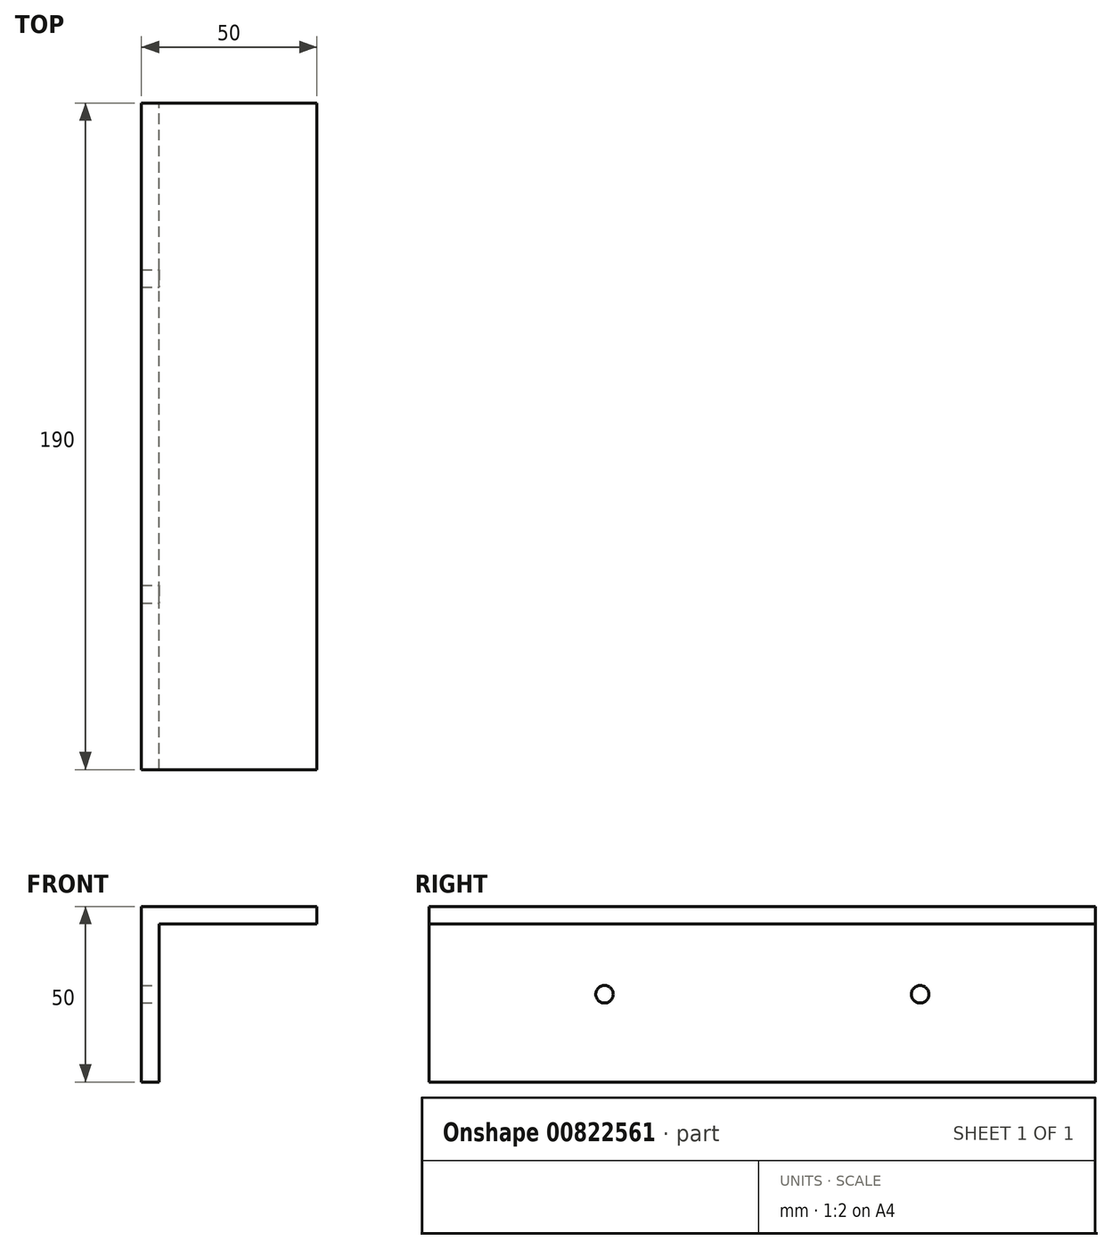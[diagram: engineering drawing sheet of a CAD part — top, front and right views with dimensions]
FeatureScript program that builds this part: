
annotation { "Feature Type Name" : "Feature", "Feature Type Description" : "" }
export const myFeature = defineFeature(function(context is Context, id is Id, definition is map)
    precondition{}
    {
        {
            var Q0;
            Q0=qCreatedBy(makeId("Front.planeOp"),FACE);
            var sketch = newSketch(context, id + "F0", { "sketchPlane" : qUnion([Q0])});
            skLineSegment(sketch, "E0", {"start": v(0, 0) * mm, "end": v(0, 50) * mm});
            skLineSegment(sketch, "E1", {"start": v(0, 50) * mm, "end": v(50, 50) * mm});
            skLineSegment(sketch, "E2", {"start": v(50, 50) * mm, "end": v(50, 45) * mm});
            skLineSegment(sketch, "E3", {"start": v(50, 45) * mm, "end": v(5, 45) * mm});
            skLineSegment(sketch, "E4", {"start": v(5, 45) * mm, "end": v(5, 0) * mm});
            skLineSegment(sketch, "E5", {"start": v(5, 0) * mm, "end": v(0, 0) * mm});
            skSolve(sketch);
        }
        {
            var Q0;
            Q0=makeQuery(id+"F0.imprint","IMPRINT",FACE,{"disambiguationData":[TD([[makeQuery(id+"F0.imprint","IMPRINT",EDGE,{"derivedFrom":sQuery(id+"F0.wireOp",EDGE,"E0")}),-1.0]])]});
            extrude(context, id + "F1", {"entities" : qUnion([Q0]), "depth" : 190 * mm, "offsetDistance" : 25 * mm});
        }
        {
            var Q0;
            Q0=makeQuery(id+"F1.opExtrude","SWEPT_FACE",FACE,{"disambiguationData":[OSD([sQuery(id+"F0.wireOp",EDGE,"E4")])]});
            var sketch = newSketch(context, id + "F2", { "sketchPlane" : qUnion([Q0])});
            skPoint(sketch, "E6", {"position": v(-140, 25) * mm});
            skPoint(sketch, "E7", {"position": v(-50, 25) * mm});
            skSolve(sketch);
        }
        {
            var Q0;
            Q0=sQuery(id+"F2.wireOp",VERTEX,"E6");
            var Q1;
            Q1=sQuery(id+"F2.wireOp",VERTEX,"E7");
            var Q2;
            Q2=makeQuery(id+"F1.opExtrude","SWEPT_BODY",BODY,{"disambiguationData":[OSD([sQuery(id+"F0.wireOp",EDGE,"E0"),sQuery(id+"F0.wireOp",EDGE,"E1"),sQuery(id+"F0.wireOp",EDGE,"E2"),sQuery(id+"F0.wireOp",EDGE,"E3"),sQuery(id+"F0.wireOp",EDGE,"E4"),sQuery(id+"F0.wireOp",EDGE,"E5")])]});
            hole(context, id + "F3", {"style" : HoleStyle.SIMPLE, "endStyle" : HoleEndStyle.THROUGH, "holeDiameter" : 5 * mm, "majorDiameter" : 5 * mm, "isTappedThrough" : true, "tappedDepth" : 12 * mm, "tapClearance" : 3, "locations" : qUnion([Q0, Q1]), "scope" : qUnion([Q2])});
        }
    });
